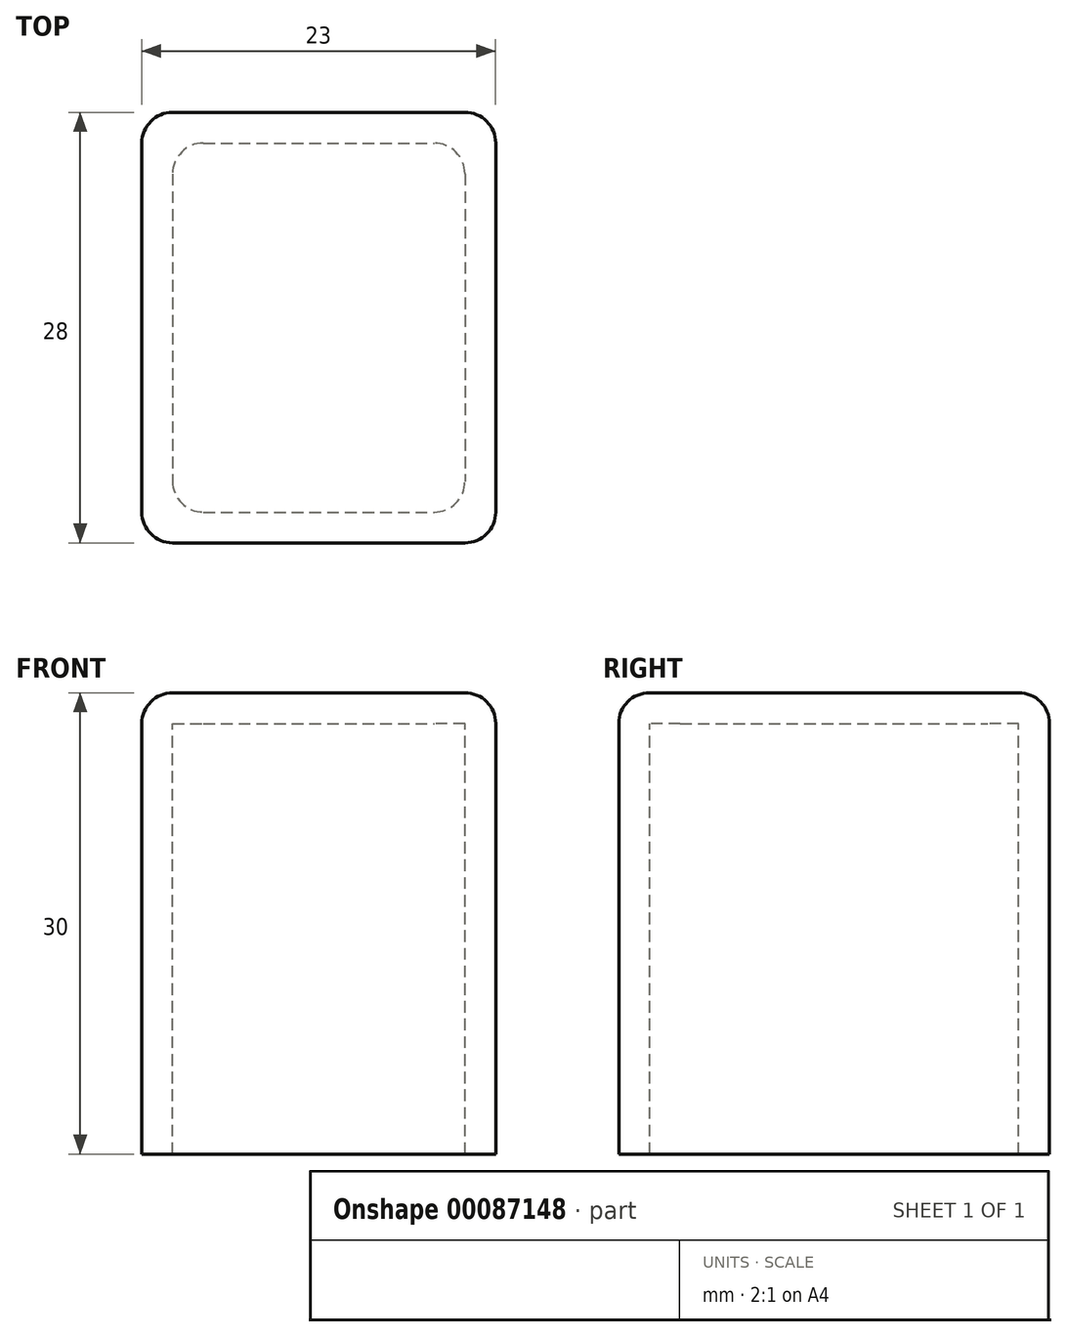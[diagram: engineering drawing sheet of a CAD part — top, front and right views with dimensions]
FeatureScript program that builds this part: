
annotation { "Feature Type Name" : "Feature", "Feature Type Description" : "" }
export const myFeature = defineFeature(function(context is Context, id is Id, definition is map)
    precondition{}
    {
        {
            var Q0;
            Q0=qCreatedBy(makeId("Top.planeOp"),FACE);
            var sketch = newSketch(context, id + "F0", { "sketchPlane" : qUnion([Q0])});
            skLineSegment(sketch, "E0.bottom", {"start": v(-53.3, 59.8) * mm, "end": v(-30.3, 59.8) * mm});
            skLineSegment(sketch, "E0.top", {"start": v(-53.3, 31.8) * mm, "end": v(-30.3, 31.8) * mm});
            skLineSegment(sketch, "E0.left", {"start": v(-53.3, 59.8) * mm, "end": v(-53.3, 31.8) * mm});
            skLineSegment(sketch, "E0.right", {"start": v(-30.3, 59.8) * mm, "end": v(-30.3, 31.8) * mm});
            skSolve(sketch);
        }
        {
            var Q0;
            Q0=makeQuery(id+"F0.imprint","IMPRINT",FACE,{"disambiguationData":[TD([[makeQuery(id+"F0.imprint","IMPRINT",EDGE,{"derivedFrom":sQuery(id+"F0.wireOp",EDGE,"E0.bottom")}),-1.0]])]});
            extrude(context, id + "F1", {"entities" : qUnion([Q0]), "depth" : 30 * mm});
        }
        {
            var Q0;
            Q0=makeQuery(id+"F1.opExtrude","SWEPT_EDGE",EDGE,{"disambiguationData":[OSD([sQuery(id+"F0.wireOp",EDGE,"E0.top"),sQuery(id+"F0.wireOp",EDGE,"E0.right")])]});
            fillet(context, id + "F2", {"entities" : qUnion([Q0]), "radius" : 2 * mm, "tangentPropagation" : true, "allowEdgeOverflow" : false});
        }
        {
            var Q0;
            Q0=makeQuery(id+"F1.opExtrude","SWEPT_EDGE",EDGE,{"disambiguationData":[OSD([sQuery(id+"F0.wireOp",EDGE,"E0.bottom"),sQuery(id+"F0.wireOp",EDGE,"E0.right")])]});
            fillet(context, id + "F3", {"entities" : qUnion([Q0]), "radius" : 2 * mm, "tangentPropagation" : true, "allowEdgeOverflow" : false});
        }
        {
            var Q0;
            Q0=makeQuery(id+"F1.opExtrude","SWEPT_EDGE",EDGE,{"disambiguationData":[OSD([sQuery(id+"F0.wireOp",EDGE,"E0.top"),sQuery(id+"F0.wireOp",EDGE,"E0.left")])]});
            fillet(context, id + "F4", {"entities" : qUnion([Q0]), "radius" : 2 * mm, "tangentPropagation" : true, "allowEdgeOverflow" : false});
        }
        {
            var Q0;
            Q0=makeQuery(id+"F1.opExtrude","SWEPT_EDGE",EDGE,{"disambiguationData":[OSD([sQuery(id+"F0.wireOp",EDGE,"E0.bottom"),sQuery(id+"F0.wireOp",EDGE,"E0.left")])]});
            fillet(context, id + "F5", {"entities" : qUnion([Q0]), "radius" : 2 * mm, "tangentPropagation" : true, "allowEdgeOverflow" : false});
        }
        {
            var Q0;
            Q0=makeQuery(id+"F1.opExtrude","CAP_EDGE",EDGE,{"disambiguationData":[OSD([sQuery(id+"F0.wireOp",EDGE,"E0.top")])],"isStart":false});
            fillet(context, id + "F6", {"entities" : qUnion([Q0]), "radius" : 2 * mm, "tangentPropagation" : true, "allowEdgeOverflow" : false});
        }
        {
            var Q0;
            Q0=makeQuery(id+"F1.opExtrude","CAP_FACE",FACE,{"disambiguationData":[OSD([sQuery(id+"F0.wireOp",EDGE,"E0.bottom"),sQuery(id+"F0.wireOp",EDGE,"E0.top"),sQuery(id+"F0.wireOp",EDGE,"E0.left"),sQuery(id+"F0.wireOp",EDGE,"E0.right")])],"isStart":true});
            shell(context, id + "F7", {"entities" : qUnion([Q0]), "thickness" : 2 * mm});
        }
        {
            var Q0;
            Q0=makeQuery(id+"F7.opShell","OFFSET_EDGE",EDGE,{"disambiguationData":[OSD([sQuery(id+"F0.wireOp",EDGE,"E0.top"),sQuery(id+"F0.wireOp",EDGE,"E0.right")])]});
            fillet(context, id + "F8", {"entities" : qUnion([Q0]), "radius" : 2 * mm, "tangentPropagation" : true, "allowEdgeOverflow" : false});
        }
        {
            var Q0;
            Q0=makeQuery(id+"F7.opShell","OFFSET_EDGE",EDGE,{"disambiguationData":[OSD([sQuery(id+"F0.wireOp",EDGE,"E0.bottom"),sQuery(id+"F0.wireOp",EDGE,"E0.right")])]});
            var Q1;
            Q1=makeQuery(id+"F7.opShell","OFFSET_EDGE",EDGE,{"disambiguationData":[OSD([sQuery(id+"F0.wireOp",EDGE,"E0.bottom"),sQuery(id+"F0.wireOp",EDGE,"E0.left")])]});
            var Q2;
            Q2=makeQuery(id+"F7.opShell","OFFSET_EDGE",EDGE,{"disambiguationData":[OSD([sQuery(id+"F0.wireOp",EDGE,"E0.top"),sQuery(id+"F0.wireOp",EDGE,"E0.left")])]});
            fillet(context, id + "F9", {"entities" : qUnion([Q0, Q1, Q2]), "radius" : 2 * mm, "tangentPropagation" : true, "allowEdgeOverflow" : false});
        }
    });
